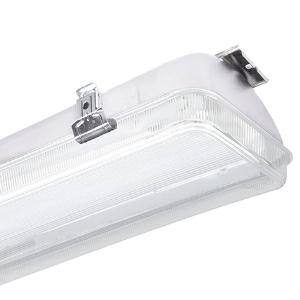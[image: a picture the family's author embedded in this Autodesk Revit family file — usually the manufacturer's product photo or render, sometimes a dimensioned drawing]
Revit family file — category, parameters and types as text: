
# Revit family: 3f_filippi_-_beta_235_75_pc_medio_3f_filippi_-_52566_-_beta_235_led_752x45_medio_l1265
name_source: partatom
category: Lighting Fixtures
units: mm (PartAtom-declared; Revit-internal decimal feet)

## family parameters
Cut with Voids When Loaded = No
Host = Face
Light Source = No
Part Type = Normal
Room Calculation Point = No
Round Connector Dimension = Use Diameter
Shared = No

## types (1)
- 3F Filippi - Beta 235 75 PC Medio (1 x LED, 13252 lm, 92 W, 4000 K)
    Apparent Load = 92 VA
    Approval mark = CE
    CIE Flux Codes = 66 89 98 98 100
    Color Rendering = 80
    Color Temperature = 4000 K
    Control Gear = Electronic ballast
    Default Elevation = 1800 mm
    Description = ILLUMINOTECHNICAL
Luminous efficiency 100% (DLOR 99%, ULOR 1%).
Initial luminous flux of the luminaire 13252 lm.
Medium symmetric distribution.
Installation Interdistance Transv.D = 1.10 x hu - Long.D = 1.10 x hu.
Tabular UGR (CIE 117 - 4H-8H; S=0.25H; 70/50/20): RUG 20.6 - 20.5.
Beam angle: 72° - 74°.
Luminous efficacy 144 lm/W.
Lifetime (L93/B10): 30000 h. (tq+25°C)
Lifetime (L90/B10): 50000 h. (tq+25°C)
Lifetime (L85/B10): 80000 h. (tq+25°C)
Lifetime (L80/B10): 100000 h. (tq+25°C)
Lifetime (L85/B10): 50000 h. (tq+45°C)
Sudden decreased luminous flux after 50000 hours: 0% (C0).
Photobiological safety in compliance with IEC/TR 62778: RG0 risk exempt, (IEC 62471).
In compliance with IEC/EN 62722-2-1 - IEC/EN 62717 standards.

SOURCE
2 linear LED modules 45W/840.
Energy efficiency class (UE 2019/2020 - UE 2019/2015): C.
CIE 13.3 Colour rendering index: CRI >80 (R9 <50%).
IES TM-30 Fidelity Index: Rf = 84 Rg = 95.
CCT nominal colour temperature 4000 K.
Colour initial tolerance (MacAdam): SDCM 3.

MECHANICAL
Single-piece housing in pressed steel, powder-coated in white epoxy-polyester.
Polycarbonate screen etched internally, V2 self-extinguishing, UV stabilised, injection moulded.
Ecologic anti-aging injected sealing gasket.
Oversized gear-tray reflector unit in highly reflective white painted hot-galvanised steel.
Methacrylate (PMMA) lenses with external flat surface.
Galvanised steel snap-lock clips for diffuser mounting (safety n° 4 per fixture).
Luminaire with limited surface temperature. - D - (EN 60598-2-24)
Dimensions: 1265x235 mm, height 135 mm. Weight 7.415 kg.
IP65 protection degree.
Mechanical strength to impacts IK10 (20 joule).
Glow-wire test resistance 850°C.

ELECTRICAL
Halogen Free electronic wiring 230V-50/60Hz, power factor 0.95, THD <25%, constant output current, class I, 1 driver.
Power of the luminaire 92 W.
ENEC - CE.
Flicker: <4%.
Luminaire compliant with EN 60598-2-22 for power supply from a centralised emergency system CPSS (Central Power Supply System), not incorporated in the luminaire - high risk areas excluded. The default power and flux are 100% in AC and 100% in DC.
Ambient temperature from -20°C to +45°C.
Temperature class T6 max 85°C.
Quick connection via M20 3P connector with 9-13 mm tightening range.
Relative humidity UR: <85%.

INSTALLATION
Ceiling / Suspended / Wall.
All accessories dedicated to this product are available on the Catalog and on our website www.3F-Filippi.com.

APPLICATIONS
Suitable product for food production plants (HACCP), IFS (Food Version 6), BRC (GSFS Food Version 7).
Dry, dusty indoor environments, subject to occasional water splashes.
Industrial environments, warehouses, environments where security locks are required on all clips, e.g. prisons (on request).
Environments in which it is necessary a total protection against falling fragments (eg environments with foodstuffs or machines with moving parts or with extreme temperature changes), use luminaires with laminated glass.
Tempered glass is not immune to falling fragments from harmless and caused by shocks or exceptionally derived from the tempering process.

WARNING
Fixture not suitable for cold stores with an ambient temperature <0°C and/or relative humidity >85%.
Luminaire designed for disposal/recycling at end-of-life.
Replaceable (LED only) light source by a professional. Replaceable control gear by a professional.
    Height = 135 mm
    Lamp = 1 x LED
    Lamp Light Flux = 13252 lm
    Lamp Power = 92 W
    Lamp count = 1
    Length = 1265 mm
    Lifetime = 50000 h
    Luminous efficacy = 144 lm/W
    Manufacturer = 3F Filippi
    ModVariant = No
    Model = 3F Filippi - 52566 - Beta 235 LED 752x45 MEDIO L1265
    Mounting Place = Ceiling
    Mounting Type = Pendant
    Number of Poles = 1
    OnlyDefault = Yes
    Power Factor = 1
    Product Name = 3F Filippi - Beta 235 75 PC Medio
    Product group = pendant luminaire
    ProductGroupID = 9
    Protection Class = Protection class I
    Protection Degree = IP 65
    RLX_Detail_Level = 1
    RLX_Emergency_Light_Flux = 0 lm
    RLX_Emergency_Type = 0
    RLX_Emergency_Type_DB = No
    RlxData = <blob elided: 94553 chars, md5=571bfa6b>
    Socket = socket
    Standby Power = 0 W
    System Light Flux = 13252 lm
    System Power = 92 W
    Type Comments = Product without accessories
    Type Image = 3ffilippi_beta_235_led_75_l655_l1265.jpg
    URL = http://relux.com
    VarID = ---
    Voltage = 0 V
    Weight = 0.00 kg
    Width = 235 mm

## geometry (parser evidence)
native form markers: Blend x4, Sweep x9
no freeform markers — native parametric forms only
